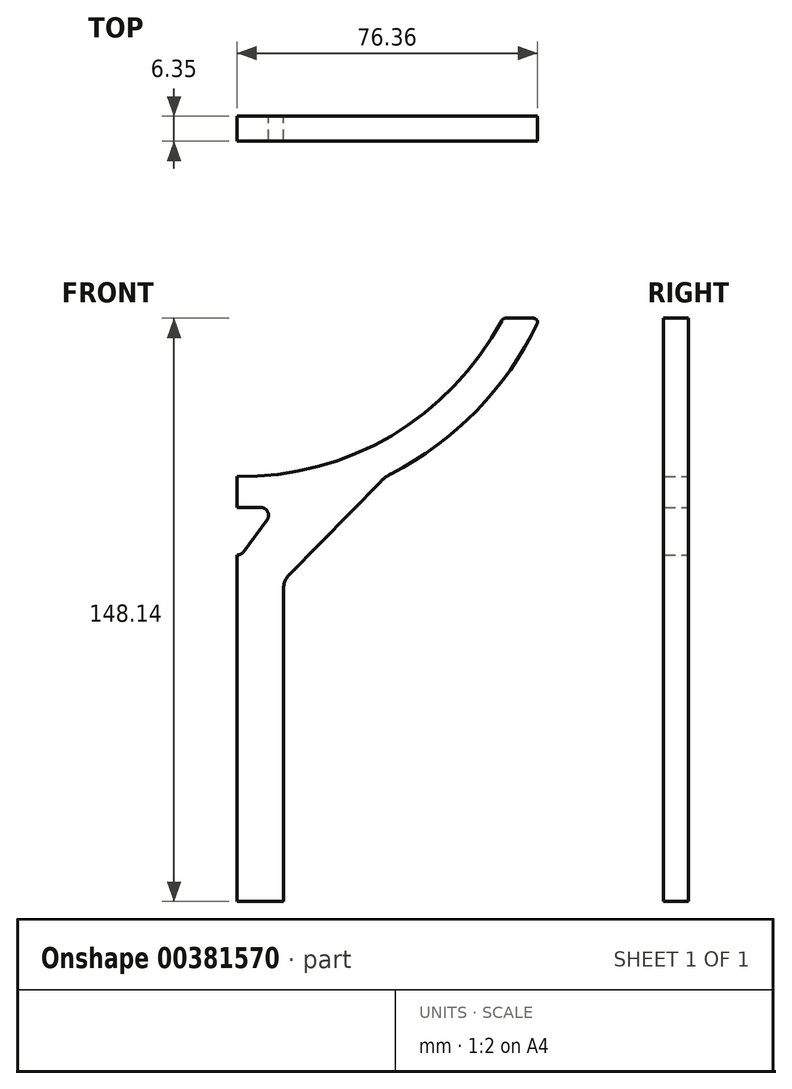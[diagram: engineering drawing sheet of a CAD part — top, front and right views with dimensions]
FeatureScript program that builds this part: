
annotation { "Feature Type Name" : "Feature", "Feature Type Description" : "" }
export const myFeature = defineFeature(function(context is Context, id is Id, definition is map)
    precondition{}
    {
        {
            var Q0;
            Q0=qCreatedBy(makeId("Front.planeOp"),FACE);
            var sketch = newSketch(context, id + "F0", { "sketchPlane" : qUnion([Q0])});
            skLineSegment(sketch, "E0", {"start": v(68.16, 21.8) * mm, "end": v(75.36, 21.8) * mm});
            skLineSegment(sketch, "E1", {"start": v(-65.86, 22.33) * mm, "end": v(-73.04, 22.33) * mm});
            skArc(sketch, "E2", {"start": v(-73.95, 20.9) * mm, "mid": v(-58.5, -1.49) * mm, "end": v(-36.64, -17.7) * mm});
            skArc(sketch, "E3.0", {"start": v(-64.98, 21.8) * mm, "mid": v(1, -18.42) * mm, "end": v(67.28, 21.27) * mm});
            skLineSegment(sketch, "E4.top", {"start": v(-9.94, -126.34) * mm, "end": v(11.86, -126.34) * mm});
            skLineSegment(sketch, "E4.left", {"start": v(-9.94, -46.77) * mm, "end": v(-9.94, -126.34) * mm});
            skArc(sketch, "E5.trimOffspring", {"start": v(39.16, -17.72) * mm, "mid": v(60.84, -1.72) * mm, "end": v(76.26, 20.37) * mm});
            skLineSegment(sketch, "E6", {"start": v(13.3, -43.3) * mm, "end": v(36.6, -19.61) * mm});
            skLineSegment(sketch, "E7", {"start": v(-11.33, -43.3) * mm, "end": v(-33.99, -19.67) * mm});
            skLineSegment(sketch, "E8.trimOffspring", {"start": v(11.86, -46.8) * mm, "end": v(11.86, -126.34) * mm});
            skPoint(sketch, "E9.visualSharp", {"position": v(11.86, -44.76) * mm});
            skArc(sketch, "E9.filletArc", {"start": v(13.3, -43.3) * mm, "mid": v(12.23, -44.9) * mm, "end": v(11.86, -46.8) * mm});
            skPoint(sketch, "E10.visualSharp", {"position": v(-9.94, -44.76) * mm});
            skArc(sketch, "E10.filletArc", {"start": v(-9.94, -46.77) * mm, "mid": v(-10.3, -44.9) * mm, "end": v(-11.33, -43.3) * mm});
            skPoint(sketch, "E11.visualSharp", {"position": v(37.76, -18.42) * mm});
            skArc(sketch, "E11.filletArc", {"start": v(39.16, -17.72) * mm, "mid": v(37.8, -18.56) * mm, "end": v(36.6, -19.61) * mm});
            skPoint(sketch, "E12.visualSharp", {"position": v(-35.18, -18.42) * mm});
            skArc(sketch, "E12.filletArc", {"start": v(-33.99, -19.67) * mm, "mid": v(-35.23, -18.57) * mm, "end": v(-36.64, -17.7) * mm});
            skLineSegment(sketch, "E13", {"start": v(-6.03, -26.26) * mm, "end": v(0, -26.26) * mm});
            skLineSegment(sketch, "E14", {"start": v(6.03, -26.26) * mm, "end": v(0, -26.26) * mm});
            skLineSegment(sketch, "E15", {"start": v(7.63, -29.46) * mm, "end": v(1.6, -37.59) * mm});
            skLineSegment(sketch, "E16", {"start": v(-1.6, -37.59) * mm, "end": v(-7.63, -29.46) * mm});
            skPoint(sketch, "E17.visualSharp", {"position": v(-10, -26.26) * mm});
            skArc(sketch, "E17.filletArc", {"start": v(-6.03, -26.26) * mm, "mid": v(-7.81, -27.36) * mm, "end": v(-7.63, -29.46) * mm});
            skPoint(sketch, "E18.visualSharp", {"position": v(10, -26.26) * mm});
            skArc(sketch, "E18.filletArc", {"start": v(7.63, -29.46) * mm, "mid": v(7.81, -27.36) * mm, "end": v(6.03, -26.26) * mm});
            skPoint(sketch, "E19.visualSharp", {"position": v(0, -39.76) * mm});
            skArc(sketch, "E19.filletArc", {"start": v(-1.6, -37.59) * mm, "mid": v(0, -38.4) * mm, "end": v(1.6, -37.59) * mm});
            skPoint(sketch, "E20.visualSharp", {"position": v(67.55, 21.8) * mm});
            skArc(sketch, "E20.filletArc", {"start": v(68.16, 21.8) * mm, "mid": v(67.64, 21.66) * mm, "end": v(67.28, 21.27) * mm});
            skPoint(sketch, "E21.visualSharp", {"position": v(76.93, 21.8) * mm});
            skArc(sketch, "E21.filletArc", {"start": v(76.26, 20.37) * mm, "mid": v(76.2, 21.34) * mm, "end": v(75.36, 21.8) * mm});
            skPoint(sketch, "E22.visualSharp", {"position": v(-65.26, 22.33) * mm});
            skArc(sketch, "E22.filletArc", {"start": v(-64.98, 21.8) * mm, "mid": v(-65.35, 22.19) * mm, "end": v(-65.86, 22.33) * mm});
            skPoint(sketch, "E23.visualSharp", {"position": v(-74.6, 22.33) * mm});
            skArc(sketch, "E23.filletArc", {"start": v(-73.04, 22.33) * mm, "mid": v(-73.88, 21.87) * mm, "end": v(-73.95, 20.9) * mm});
            skLineSegment(sketch, "E24", {"start": v(0, 0) * mm, "end": v(0, -178.26) * mm});
            skSolve(sketch);
        }
        {
            var Q0;
            Q0=makeQuery(id+"F0.imprint","IMPRINT",FACE,{"disambiguationData":[TD([[makeQuery(id+"F0.imprint","IMPRINT",EDGE,{"derivedFrom":sQuery(id+"F0.wireOp",EDGE,"E0")}),-1.0]])]});
            extrude(context, id + "F1", {"entities" : qUnion([Q0]), "depth" : 6.35 * mm});
        }
    });
